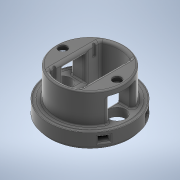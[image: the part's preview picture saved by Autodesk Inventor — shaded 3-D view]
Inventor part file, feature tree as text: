
AUTODESK INVENTOR PART (.ipt)
format: ipt  version: 2020 (Build 240168000, 168)  size: 718,336 bytes
history: native  units: in
note: dims shown in document units (in); Inventor stores cm internally (conversion verified against a paired STEP export)
features: sketch x11, extrude x7, revolve x2, hole x2, plane x2, fillet x2
ambient origin geometry x8: Origin, YZ Plane, XZ Plane, XY Plane, X Axis, Y Axis, Z Axis, Center Point
bodies: Solid1 (feature_tree)
feature tree (26):
  revolve  "Revolution1"  [1 undecoded]
  hole  "Hole1"  [1 undecoded]
  extrude  "Extrusion1"  Depth=2.4in
  plane  "Work Plane1"
  extrude  "Extrusion3"  Depth=1.0in
  extrude  "Extrusion4"  Depth=2.4in
  extrude  "Extrusion5"  Depth=0.3125in TaperAngle=0.0deg
  plane  "Work Plane2"
  extrude  "Extrusion6"  Depth=1.875in
  hole  "Hole2"  [1 undecoded]
  revolve  "Revolution2"  [1 undecoded]
  extrude  "Extrusion8"  Depth=0.0625in
  fillet  "Fillet14"  Radius=0.625in
  fillet  "Fillet15"  Radius=0.75in
  extrude  "Extrusion14"  Depth=0.0625in TaperAngle=0.0deg
  sketch  "Sketch1"  dims[d3=1.5in d4=0.125in]
  sketch  "Sketch2"  dims[d5=1.75in d6=0.1in]
  sketch  "Sketch3"  dims[d8=90.0deg d9=2.4in]
  sketch  "Sketch5"  dims[d10=1.5in]
  sketch  "Sketch6"  dims[d11=0.2031in d12=0.75in d13=0.3125in d14=0.875in d15=0.5635in d16=0.5in d17=0.0in d18=1.0in]
  sketch  "Sketch7"  dims[d19=0.125in d20=2.4in]
  sketch  "Sketch8"  dims[d21=2.0in d22=0.3125in d23=0.0in]
  sketch  "Sketch9"  dims[d28=0.55in d29=1.875in]
  sketch  "Sketch10"  dims[d30=-0.25in d31=2.4in]
  sketch  "Sketch13"  dims[d32=1.0in d33=0.375in d34=0.0in]
  sketch  "Sketch21"  dims[d35=1.375in d36=2.25in d37=0.625in d38=0.0in d39=0.75in d40=0.75in d41=0.0in d42=-0.375in d43=0.375in d44=0.25in d45=0.0in d46=0.375in d47=0.75in d48=0.5in d49=0.188in d50=0.5635in d51=1.0in d52=0.8108in d56=0.125in d57=1.75in d58=0.02in d59=90.0deg d67=1.781in d68=0.0in d108=0.125in d109=0.0625in d111=1.75in d112=0.125in d113=0.5in d114=0.0in]
note: 4 required parameter values undecoded (feature->parameter linkage not recoverable at this tier; creation-order binding heuristic only, values carry confidence <= 0.55)